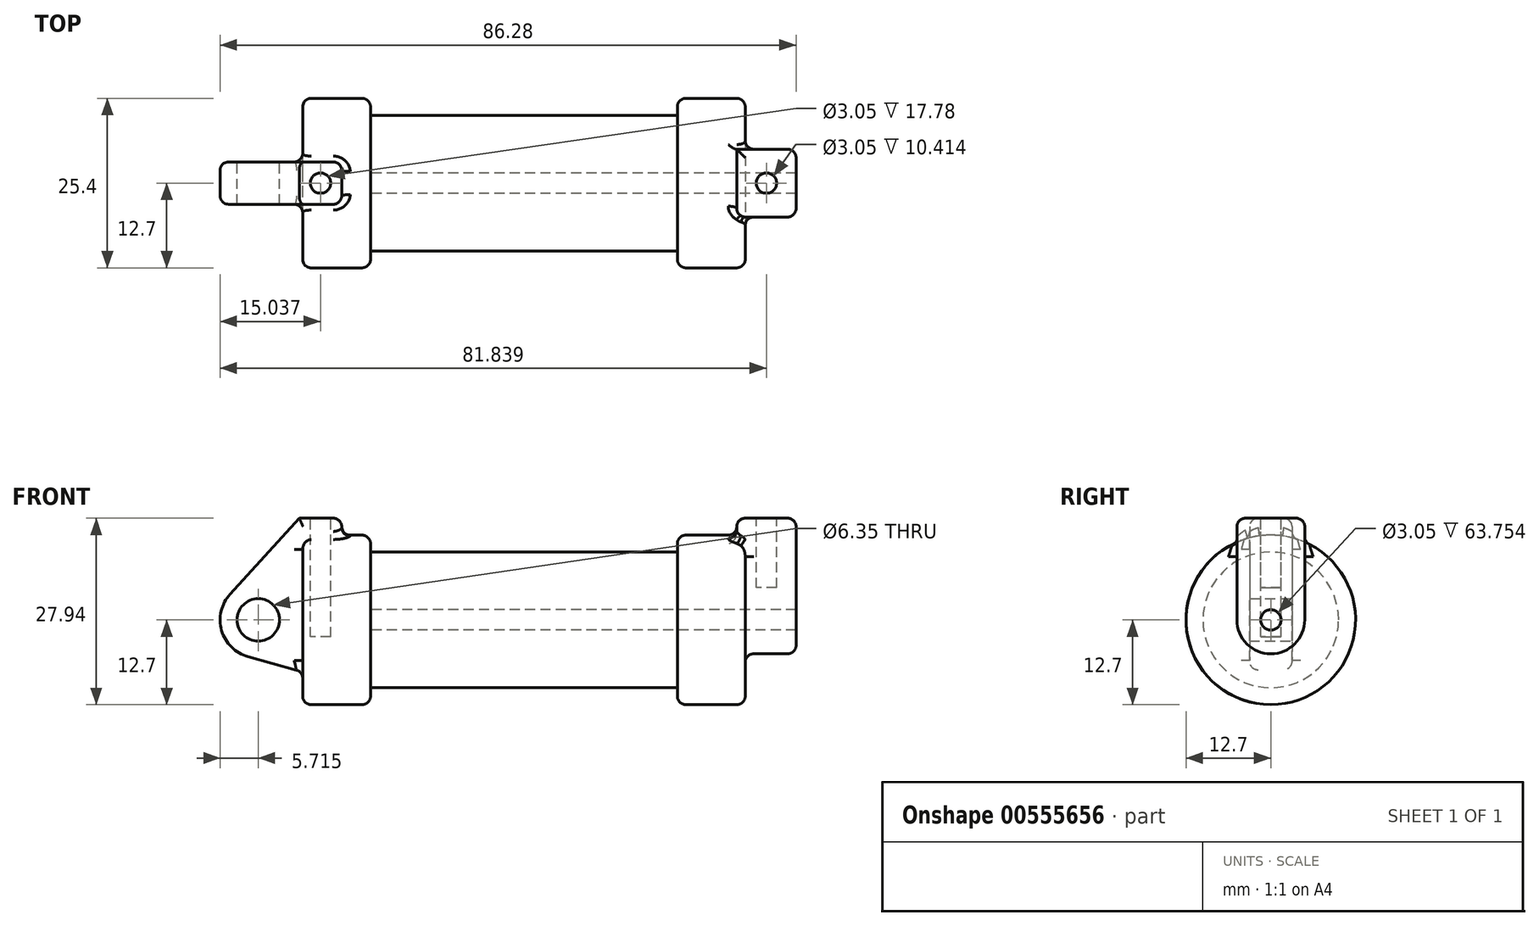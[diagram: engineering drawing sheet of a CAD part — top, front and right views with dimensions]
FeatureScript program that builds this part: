
annotation { "Feature Type Name" : "Feature", "Feature Type Description" : "" }
export const myFeature = defineFeature(function(context is Context, id is Id, definition is map)
    precondition{}
    {
        {
            var Q0;
            Q0=qCreatedBy(makeId("Front.planeOp"),FACE);
            var sketch = newSketch(context, id + "F0", { "sketchPlane" : qUnion([Q0])});
            skLineSegment(sketch, "E0", {"start": v(0, 0) * mm, "end": v(0, 12.7) * mm});
            skLineSegment(sketch, "E1", {"start": v(0, 12.7) * mm, "end": v(10.16, 12.7) * mm});
            skLineSegment(sketch, "E2", {"start": v(10.16, 12.7) * mm, "end": v(10.16, 10.16) * mm});
            skLineSegment(sketch, "E3", {"start": v(10.16, 10.16) * mm, "end": v(56.13, 10.16) * mm});
            skLineSegment(sketch, "E4", {"start": v(56.13, 10.16) * mm, "end": v(56.13, 12.7) * mm});
            skLineSegment(sketch, "E5", {"start": v(56.13, 12.7) * mm, "end": v(66.3, 12.7) * mm});
            skLineSegment(sketch, "E6", {"start": v(66.3, 12.7) * mm, "end": v(66.3, 0) * mm});
            skLineSegment(sketch, "E7", {"start": v(66.3, 0) * mm, "end": v(0, 0) * mm});
            skLineSegment(sketch, "E8", {"start": v(5.84, 15.24) * mm, "end": v(-0.5, 15.24) * mm});
            skLineSegment(sketch, "E9", {"start": v(-0.5, 15.24) * mm, "end": v(-10.88, 3.85) * mm});
            skLineSegment(sketch, "E10", {"start": v(0, 0) * mm, "end": v(-6.65, 0) * mm});
            skCircle(sketch, "E11", {"center": v(-6.65, 0) * mm, "radius": 5.72 * mm});
            skCircle(sketch, "E12", {"center": v(-6.65, 0) * mm, "radius": 3.18 * mm});
            skLineSegment(sketch, "E13", {"start": v(5.84, 15.24) * mm, "end": v(5.84, -9.4) * mm});
            skLineSegment(sketch, "E14", {"start": v(5.84, -9.4) * mm, "end": v(-8.18, -5.5) * mm});
            skSolve(sketch);
        }
        {
            var Q0;
            {var subQ0=sQuery(id+"F0.wireOp",EDGE,"E2");Q0=makeQuery(id+"F0.imprint","IMPRINT",FACE,{"disambiguationData":[TD([[makeQuery(id+"F0.imprint","IMPRINT",EDGE,{"derivedFrom":subQ0}),-1.0]])]});}
            var Q1;
            {var subQ0=sQuery(id+"F0.wireOp",EDGE,"E0");Q1=makeQuery(id+"F0.imprint","IMPRINT",FACE,{"disambiguationData":[TD([[makeQuery(id+"F0.imprint","IMPRINT",EDGE,{"derivedFrom":subQ0}),-1.0]])]});}
            var Q2;
            Q2=sQuery(id+"F0.wireOp",EDGE,"E7");
            revolve(context, id + "F1", {"entities" : qUnion([Q0, Q1]), "axis" : qUnion([Q2]), "revolveType" : RevolveType.FULL});
        }
        {
            var Q0;
            {var subQ0=sQuery(id+"F0.wireOp",EDGE,"E0");Q0=makeQuery(id+"F0.imprint","IMPRINT",FACE,{"disambiguationData":[TD([[makeQuery(id+"F0.imprint","IMPRINT",EDGE,{"derivedFrom":subQ0}),-1.0]])]});}
            var Q1;
            {var subQ1=sQuery(id+"F0.wireOp",EDGE,"E0");Q1=makeQuery(id+"F0.imprint","IMPRINT",FACE,{"disambiguationData":[TD([[makeQuery(id+"F0.imprint","IMPRINT",EDGE,{"derivedFrom":subQ1}),1.0]])]});}
            var Q2;
            {var subQ0=sQuery(id+"F0.wireOp",EDGE,"E14");Q2=makeQuery(id+"F0.imprint","IMPRINT",FACE,{"disambiguationData":[TD([[makeQuery(id+"F0.imprint","IMPRINT",EDGE,{"derivedFrom":subQ0}),-1.0]])]});}
            var Q3;
            {var subQ5=sQuery(id+"F0.wireOp",EDGE,"E12");Q3=makeQuery(id+"F0.imprint","IMPRINT",FACE,{"disambiguationData":[TD([[makeQuery(id+"F0.imprint","IMPRINT",EDGE,{"derivedFrom":subQ5}),-1.0]])]});}
            extrude(context, id + "F2", {"entities" : qUnion([Q0, Q1, Q2, Q3]), "operationType" : NewBodyOperationType.ADD, "endBound" : BoundingType.SYMMETRIC, "depth" : 6.35 * mm, "offsetDistance" : 25.4 * mm});
        }
        {
            var Q0;
            Q0=makeQuery(id+"F1.opRevolve","SWEPT_FACE",FACE,{"disambiguationData":[OSD([sQuery(id+"F0.wireOp",EDGE,"E6")])]});
            var sketch = newSketch(context, id + "F3", { "sketchPlane" : qUnion([Q0])});
            skCircle(sketch, "E15", {"center": v(0, 0) * mm, "radius": 1.52 * mm});
            skCircle(sketch, "E16", {"center": v(0, 0) * mm, "radius": 5.08 * mm});
            skLineSegment(sketch, "E17", {"start": v(-5.08, 0) * mm, "end": v(-5.08, 15.24) * mm});
            skLineSegment(sketch, "E18", {"start": v(-5.08, 15.24) * mm, "end": v(5.08, 15.24) * mm});
            skLineSegment(sketch, "E19", {"start": v(5.08, 15.24) * mm, "end": v(5.08, 0) * mm});
            skSolve(sketch);
        }
        {
            var Q0;
            {var subQ0=sQuery(id+"F3.wireOp",EDGE,"E18");Q0=makeQuery(id+"F3.imprint","IMPRINT",FACE,{"disambiguationData":[TD([[makeQuery(id+"F3.imprint","IMPRINT",EDGE,{"derivedFrom":subQ0}),-1.0]])]});}
            var Q1;
            {var subQ0=sQuery(id+"F3.wireOp",EDGE,"E17");var subQ1=sQuery(id+"F3.wireOp",EDGE,"E16");var subQ2=makeQuery(id+"F3.imprint","INTERSECT",VERTEX,{"derivedFrom":[subQ1,subQ0]});Q1=makeQuery(id+"F3.imprint","IMPRINT",FACE,{"disambiguationData":[TD([[makeQuery(id+"F3.imprint","IMPRINT",EDGE,{"disambiguationData":[TD([[subQ2,1.0]])],"derivedFrom":subQ1}),-1.0]])]});}
            var Q2;
            Q2=makeQuery(id+"F3.imprint","IMPRINT",FACE,{"disambiguationData":[TD([[makeQuery(id+"F3.imprint","IMPRINT",EDGE,{"derivedFrom":sQuery(id+"F3.wireOp",EDGE,"E15")}),-1.0]])]});
            extrude(context, id + "F4", {"entities" : qUnion([Q0, Q1, Q2]), "operationType" : NewBodyOperationType.ADD, "depth" : 7.62 * mm, "offsetDistance" : 25.4 * mm, "hasSecondDirection" : true, "secondDirectionOppositeDirection" : true, "secondDirectionDepth" : 1.27 * mm});
        }
        {
            var Q0;
            Q0=makeQuery(id+"F3.imprint","IMPRINT",FACE,{"disambiguationData":[TD([[makeQuery(id+"F3.imprint","IMPRINT",EDGE,{"derivedFrom":sQuery(id+"F3.wireOp",EDGE,"E15")}),1.0]])]});
            var Q1;
            Q1=makeQuery(id+"F1.opRevolve","SWEPT_FACE",FACE,{"disambiguationData":[OSD([sQuery(id+"F0.wireOp",EDGE,"E2")])]});
            extrude(context, id + "F5", {"entities" : qUnion([Q0]), "operationType" : NewBodyOperationType.REMOVE, "endBound" : BoundingType.UP_TO_SURFACE, "oppositeDirection" : true, "depth" : 25.4 * mm, "endBoundEntityFace" : qUnion([Q1]), "offsetDistance" : 25.4 * mm});
        }
        {
            var Q0;
            Q0=makeQuery(id+"F2.opExtrude","SWEPT_FACE",FACE,{"disambiguationData":[OSD([sQuery(id+"F0.wireOp",EDGE,"E8")])]});
            var sketch = newSketch(context, id + "F6", { "sketchPlane" : qUnion([Q0])});
            skCircle(sketch, "E20", {"center": v(2.67, 0) * mm, "radius": 1.52 * mm});
            skPoint(sketch, "E20.centerSnap0", {"position": v(5.84, 0) * mm});
            skPoint(sketch, "E20.centerSnap1", {"position": v(2.67, 3.18) * mm});
            skSolve(sketch);
        }
        {
            var Q0;
            Q0=makeQuery(id+"F4.opExtrude","SWEPT_FACE",FACE,{"disambiguationData":[OSD([sQuery(id+"F3.wireOp",EDGE,"E18")])]});
            var sketch = newSketch(context, id + "F7", { "sketchPlane" : qUnion([Q0])});
            skCircle(sketch, "E21", {"center": v(69.47, 0) * mm, "radius": 1.52 * mm});
            skPoint(sketch, "E21.centerSnap0", {"position": v(69.47, 5.08) * mm});
            skPoint(sketch, "E21.centerSnap1", {"position": v(65.02, 0) * mm});
            skSolve(sketch);
        }
        {
            var Q0;
            Q0=makeQuery(id+"F6.imprint","IMPRINT",FACE,{"disambiguationData":[TD([[makeQuery(id+"F6.imprint","IMPRINT",EDGE,{"derivedFrom":sQuery(id+"F6.wireOp",EDGE,"E20")}),1.0]])]});
            extrude(context, id + "F8", {"entities" : qUnion([Q0]), "operationType" : NewBodyOperationType.REMOVE, "oppositeDirection" : true, "depth" : 17.78 * mm, "offsetDistance" : 25.4 * mm});
        }
        {
            var Q0;
            Q0=makeQuery(id+"F7.imprint","IMPRINT",FACE,{"disambiguationData":[TD([[makeQuery(id+"F7.imprint","IMPRINT",EDGE,{"derivedFrom":sQuery(id+"F7.wireOp",EDGE,"E21")}),1.0]])]});
            extrude(context, id + "F9", {"entities" : qUnion([Q0]), "operationType" : NewBodyOperationType.REMOVE, "oppositeDirection" : true, "depth" : 10.4 * mm, "offsetDistance" : 25.4 * mm});
        }
        {
            var Q0;
            Q0=makeQuery(id+"F1.opRevolve","SWEPT_EDGE",EDGE,{"disambiguationData":[OSD([sQuery(id+"F0.wireOp",EDGE,"E1"),sQuery(id+"F0.wireOp",EDGE,"E2")])]});
            var Q1;
            Q1=makeQuery(id+"F1.opRevolve","SWEPT_EDGE",EDGE,{"disambiguationData":[OSD([sQuery(id+"F0.wireOp",EDGE,"E0"),sQuery(id+"F0.wireOp",EDGE,"E1")])]});
            var Q2;
            Q2=makeQuery(id+"F1.opRevolve","SWEPT_EDGE",EDGE,{"disambiguationData":[OSD([sQuery(id+"F0.wireOp",EDGE,"E4"),sQuery(id+"F0.wireOp",EDGE,"E5")])]});
            var Q3;
            Q3=makeQuery(id+"F1.opRevolve","SWEPT_EDGE",EDGE,{"disambiguationData":[OSD([sQuery(id+"F0.wireOp",EDGE,"E5"),sQuery(id+"F0.wireOp",EDGE,"E6")])]});
            fillet(context, id + "F10", {"entities" : qUnion([Q0, Q1, Q2, Q3]), "radius" : 1.27 * mm, "tangentPropagation" : true, "allowEdgeOverflow" : false});
        }
        {
            var Q0;
            Q0=makeQuery(id+"F2.opExtrude","CAP_EDGE",EDGE,{"disambiguationData":[OSD([sQuery(id+"F0.wireOp",EDGE,"E9")])],"isStart":true});
            var Q1;
            Q1=makeQuery(id+"F2.opExtrude","CAP_EDGE",EDGE,{"disambiguationData":[OSD([sQuery(id+"F0.wireOp",EDGE,"E9")])],"isStart":false});
            var Q2;
            Q2=makeQuery(id+"F2.opExtrude","CAP_EDGE",EDGE,{"disambiguationData":[OSD([sQuery(id+"F0.wireOp",EDGE,"E14")])],"isStart":true});
            var Q3;
            Q3=makeQuery(id+"F2.opExtrude","CAP_EDGE",EDGE,{"disambiguationData":[OSD([sQuery(id+"F0.wireOp",EDGE,"E11")])],"isStart":true});
            var Q4;
            Q4=makeQuery(id+"F2.opExtrude","CAP_EDGE",EDGE,{"disambiguationData":[OSD([sQuery(id+"F0.wireOp",EDGE,"E11")])],"isStart":false});
            var Q5;
            Q5=makeQuery(id+"F2.opExtrude","CAP_EDGE",EDGE,{"disambiguationData":[OSD([sQuery(id+"F0.wireOp",EDGE,"E14")])],"isStart":false});
            var Q6;
            Q6=makeQuery(id+"F2.opExtrude","CAP_EDGE",EDGE,{"disambiguationData":[OSD([sQuery(id+"F0.wireOp",EDGE,"E8")])],"isStart":false});
            var Q7;
            Q7=makeQuery(id+"F2.opExtrude","SWEPT_EDGE",EDGE,{"disambiguationData":[OSD([sQuery(id+"F0.wireOp",EDGE,"E8"),sQuery(id+"F0.wireOp",EDGE,"E13")])]});
            var Q8;
            Q8=makeQuery(id+"F2.opExtrude","CAP_EDGE",EDGE,{"disambiguationData":[OSD([sQuery(id+"F0.wireOp",EDGE,"E8")])],"isStart":true});
            var Q9;
            Q9=makeQuery(id+"F2.opExtrude","CAP_EDGE",EDGE,{"disambiguationData":[OSD([sQuery(id+"F0.wireOp",EDGE,"E13")])],"isStart":true});
            var Q10;
            Q10=makeQuery(id+"F2.opExtrude","CAP_EDGE",EDGE,{"disambiguationData":[OSD([sQuery(id+"F0.wireOp",EDGE,"E13")])],"isStart":false});
            fillet(context, id + "F11", {"entities" : qUnion([Q0, Q1, Q2, Q3, Q4, Q5, Q6, Q7, Q8, Q9, Q10]), "radius" : 1.27 * mm, "tangentPropagation" : true, "allowEdgeOverflow" : false});
        }
        {
            var Q0;
            Q0=makeQuery(id+"F4.opExtrude","CAP_EDGE",EDGE,{"disambiguationData":[OSD([sQuery(id+"F3.wireOp",EDGE,"E17")])],"isStart":true});
            var Q1;
            Q1=makeQuery(id+"F4.opExtrude","SWEPT_EDGE",EDGE,{"disambiguationData":[OSD([sQuery(id+"F3.wireOp",EDGE,"E17"),sQuery(id+"F3.wireOp",EDGE,"E18")])]});
            var Q2;
            Q2=makeQuery(id+"F4.opExtrude","CAP_EDGE",EDGE,{"disambiguationData":[OSD([sQuery(id+"F3.wireOp",EDGE,"E17")])],"isStart":false});
            var Q3;
            Q3=makeQuery(id+"F4.opExtrude","CAP_EDGE",EDGE,{"disambiguationData":[OSD([sQuery(id+"F3.wireOp",EDGE,"E16")])],"isStart":false});
            var Q4;
            Q4=makeQuery(id+"F4.opExtrude","CAP_EDGE",EDGE,{"disambiguationData":[OSD([sQuery(id+"F3.wireOp",EDGE,"E19")])],"isStart":false});
            var Q5;
            Q5=makeQuery(id+"F4.opExtrude","SWEPT_EDGE",EDGE,{"disambiguationData":[OSD([sQuery(id+"F3.wireOp",EDGE,"E18"),sQuery(id+"F3.wireOp",EDGE,"E19")])]});
            var Q6;
            Q6=makeQuery(id+"F4.opExtrude","CAP_EDGE",EDGE,{"disambiguationData":[OSD([sQuery(id+"F3.wireOp",EDGE,"E18")])],"isStart":true});
            var Q7;
            Q7=makeQuery(id+"F4.opExtrude","CAP_EDGE",EDGE,{"disambiguationData":[OSD([sQuery(id+"F3.wireOp",EDGE,"E18")])],"isStart":false});
            fillet(context, id + "F12", {"entities" : qUnion([Q0, Q1, Q2, Q3, Q4, Q5, Q6, Q7]), "radius" : 1.27 * mm, "tangentPropagation" : true, "allowEdgeOverflow" : false});
        }
        {
            var Q0;
            {var subQ0=sQuery(id+"F3.wireOp",EDGE,"E18");Q0=makeQuery(id+"F12.opFillet","BLEND_EDGE",EDGE,{"blendedFrom":[makeQuery(id+"F4.opExtrude","CAP_EDGE",EDGE,{"disambiguationData":[OSD([subQ0])],"isStart":true}),makeQuery(id+"F4.opExtrude","CAP_FACE",FACE,{"disambiguationData":[OSD([sQuery(id+"F3.wireOp",EDGE,"E15"),sQuery(id+"F3.wireOp",EDGE,"E16"),sQuery(id+"F3.wireOp",EDGE,"E17"),subQ0,sQuery(id+"F3.wireOp",EDGE,"E19")])],"isStart":true})],"blendedInto":[makeQuery(id+"F4.opExtrude","CAP_FACE",FACE,{"disambiguationData":[OSD([sQuery(id+"F3.wireOp",EDGE,"E15"),sQuery(id+"F3.wireOp",EDGE,"E16"),sQuery(id+"F3.wireOp",EDGE,"E17"),subQ0,sQuery(id+"F3.wireOp",EDGE,"E19")])],"isStart":true})]});}
            var Q1;
            Q1=makeQuery(id+"F4.boolean.opBoolean","INTERSECT",EDGE,{"derivedFrom":[makeQuery(id+"F1.opRevolve","SWEPT_FACE",FACE,{"disambiguationData":[OSD([sQuery(id+"F0.wireOp",EDGE,"E5")])]}),makeQuery(id+"F4.opExtrude","CAP_FACE",FACE,{"disambiguationData":[OSD([sQuery(id+"F3.wireOp",EDGE,"E15"),sQuery(id+"F3.wireOp",EDGE,"E16"),sQuery(id+"F3.wireOp",EDGE,"E17"),sQuery(id+"F3.wireOp",EDGE,"E18"),sQuery(id+"F3.wireOp",EDGE,"E19")])],"isStart":true})]});
            var Q2;
            Q2=makeQuery(id+"F2.boolean.opBoolean","INTERSECT",EDGE,{"derivedFrom":[makeQuery(id+"F1.opRevolve","SWEPT_FACE",FACE,{"disambiguationData":[OSD([sQuery(id+"F0.wireOp",EDGE,"E1")])]}),makeQuery(id+"F2.opExtrude","SWEPT_FACE",FACE,{"disambiguationData":[OSD([sQuery(id+"F0.wireOp",EDGE,"E13")])]})]});
            fillet(context, id + "F13", {"entities" : qUnion([Q0, Q1, Q2]), "radius" : 1.27 * mm, "tangentPropagation" : true, "allowEdgeOverflow" : false});
        }
    });
